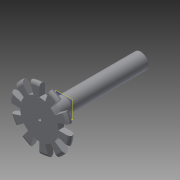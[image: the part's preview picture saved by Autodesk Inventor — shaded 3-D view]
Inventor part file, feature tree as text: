
AUTODESK INVENTOR PART (.ipt)
format: ipt  version: 2015 (Build 190159000, 159)  size: 217,088 bytes
history: native  units: mm
features: extrude x6, sketch x6, fillet x4, pattern_circular x1, plane x1
ambient origin geometry x8: Origin, YZ Plane, XZ Plane, XY Plane, X Axis, Y Axis, Z Axis, Center Point
bodies: Solid1 (feature_tree)
feature tree (18):
  extrude  "Extrusion1"  Depth=3.0mm TaperAngle=0.0deg
  fillet  "Fillet1"  Radius=2.0mm
  pattern_circular  "Circular Pattern1"  Count=10 Angle=360.0deg
  extrude  "Extrusion2"  Depth=3.0mm TaperAngle=0.0deg
  fillet  "Fillet2"  Radius=2.0mm
  fillet  "Fillet3"  Radius=2.0mm
  fillet  "Fillet4"  Radius=2.0mm
  extrude  "Extrusion3"  Depth=8.0mm TaperAngle=0.0deg
  extrude  "Extrusion4"  Depth=40.0mm TaperAngle=0.0deg
  extrude  "Extrusion5"  Depth=10.0mm TaperAngle=0.0deg
  plane  "Work Plane1"
  extrude  "Extrusion6"  Depth=40.0mm
  sketch  "Sketch1"  dims[d1=3.141593mm d2=3.0mm d3=0.0mm d4=2.0mm d5=100.0mm d6=360.0deg]
  sketch  "Sketch2"  dims[d8=20.0mm d9=3.0mm d10=0.0mm d11=2.0mm d12=2.0mm d13=2.0mm]
  sketch  "Sketch3"  dims[d14=1.8mm d15=8.0mm d16=0.0mm]
  sketch  "Sketch4"  dims[d17=8.2mm d18=40.0mm d19=0.0mm]
  sketch  "Sketch5"  dims[d20=8.2mm d21=10.0mm d22=0.0mm]
  sketch  "Sketch6"  dims[d23=-40.0mm d24=5.2mm d25=40.0mm d26=0.0mm]
